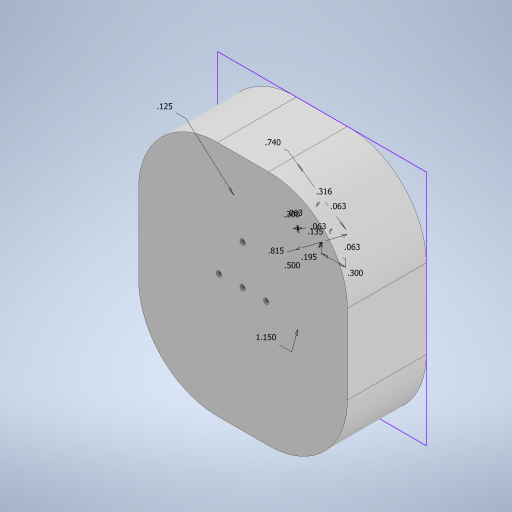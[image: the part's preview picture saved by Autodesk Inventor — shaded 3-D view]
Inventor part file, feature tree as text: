
AUTODESK INVENTOR PART (.ipt)
format: ipt  version: 2023 (Build 270158000, 158)  size: 485,376 bytes
history: native  units: in
note: dims shown in document units (in); Inventor stores cm internally (conversion verified against a paired STEP export)
features: extrude x3, fillet x2, sketch x1
ambient origin geometry x8: Origin, YZ Plane, XZ Plane, XY Plane, X Axis, Y Axis, Z Axis, Center Point
bodies: Body1 (feature_tree)
feature tree (6):
  sketch  "Sketch1"  dims[d3=0.866in d15=0.75in d20=0.316in d37=0.75in d44=0.125in d57=0.74in d70=0.135in d73=1.15in d76=0.3in d77=0.3in d84=0.5in d85=0.195in d97=0.0625in d98=0.0625in d99=0.0625in d100=0.0625in d101=1.0in d102=0.0in d103=0.76in d104=0.0in d105=0.45in d106=0.0in d107=0.04in d108=1.0in d109=0.815in]
  extrude  "Extrusion22"  Depth=1.0in
  extrude  "Extrusion23"  Depth=1.0in
  extrude  "Extrusion24"  Depth=0.125in
  fillet  "Fillet4"  Radius=0.74in
  fillet  "Fillet5"  Radius=0.135in
